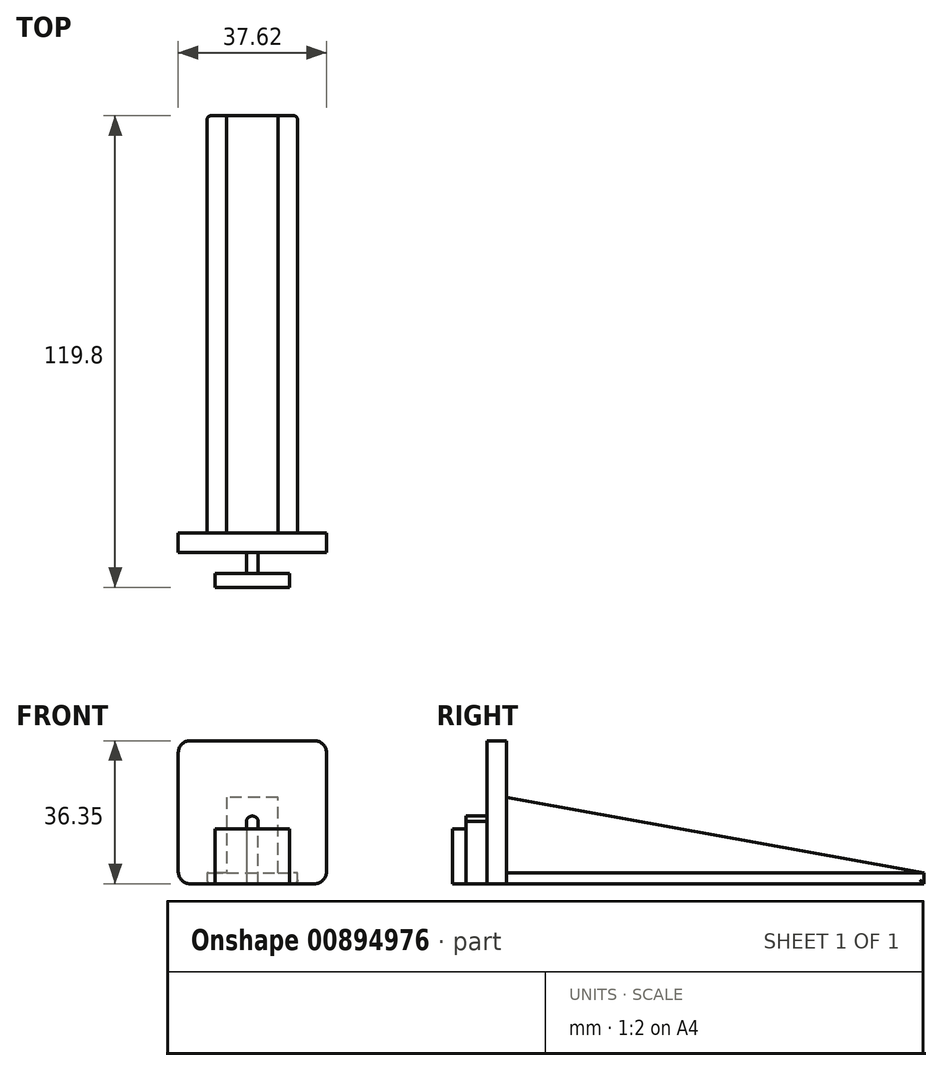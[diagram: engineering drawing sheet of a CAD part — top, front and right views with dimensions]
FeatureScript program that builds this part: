
annotation { "Feature Type Name" : "Feature", "Feature Type Description" : "" }
export const myFeature = defineFeature(function(context is Context, id is Id, definition is map)
    precondition{}
    {
        {
            var Q0;
            Q0=qCreatedBy(makeId("Front.planeOp"),FACE);
            var sketch = newSketch(context, id + "F0", { "sketchPlane" : qUnion([Q0])});
            skLineSegment(sketch, "E0", {"start": v(0, 0) * mm, "end": v(0, 36.35) * mm});
            skLineSegment(sketch, "E1", {"start": v(0, 36.35) * mm, "end": v(37.62, 36.35) * mm});
            skLineSegment(sketch, "E2", {"start": v(37.62, 36.35) * mm, "end": v(37.62, 0) * mm});
            skLineSegment(sketch, "E3", {"start": v(37.62, 0) * mm, "end": v(0, 0) * mm});
            skSolve(sketch);
        }
        {
            var Q0;
            Q0 = qSketchRegion(id + "F0", true);
            extrude(context, id + "F1", {"entities" : qUnion([Q0]), "depth" : 5 * mm, "offsetDistance" : 25 * mm});
        }
        {
            var Q0;
            Q0=makeQuery(id+"F1.opExtrude","CAP_FACE",FACE,{"disambiguationData":[OSD([sQuery(id+"F0.wireOp",EDGE,"E0"),sQuery(id+"F0.wireOp",EDGE,"E1"),sQuery(id+"F0.wireOp",EDGE,"E2"),sQuery(id+"F0.wireOp",EDGE,"E3")])],"isStart":false});
            var sketch = newSketch(context, id + "F2", { "sketchPlane" : qUnion([Q0])});
            skLineSegment(sketch, "E4", {"start": v(17.3, 0) * mm, "end": v(20.31, 0) * mm});
            skLineSegment(sketch, "E5", {"start": v(20.3, 0) * mm, "end": v(20.3, 17.2) * mm});
            skLineSegment(sketch, "E6", {"start": v(20.3, 17.2) * mm, "end": v(17.31, 17.2) * mm});
            skLineSegment(sketch, "E7", {"start": v(17.3, 17.2) * mm, "end": v(17.3, 0) * mm});
            skPoint(sketch, "E8", {"position": v(18.8, 0) * mm});
            skSolve(sketch);
        }
        {
            var Q0;
            Q0=makeQuery(id+"F2.imprint","IMPRINT",FACE,{"disambiguationData":[TD([[makeQuery(id+"F2.imprint","IMPRINT",EDGE,{"derivedFrom":sQuery(id+"F2.wireOp",EDGE,"E4")}),-1.0]])]});
            extrude(context, id + "F3", {"entities" : qUnion([Q0]), "operationType" : NewBodyOperationType.ADD, "depth" : 5.3 * mm, "offsetDistance" : 25 * mm});
        }
        {
            var Q0;
            Q0=makeQuery(id+"F3.opExtrude","CAP_FACE",FACE,{"disambiguationData":[OSD([sQuery(id+"F2.wireOp",EDGE,"E4"),sQuery(id+"F2.wireOp",EDGE,"E5"),sQuery(id+"F2.wireOp",EDGE,"E6"),sQuery(id+"F2.wireOp",EDGE,"E7")])],"isStart":false});
            var sketch = newSketch(context, id + "F4", { "sketchPlane" : qUnion([Q0])});
            skLineSegment(sketch, "E9", {"start": v(9.3, 0) * mm, "end": v(28.31, 0) * mm});
            skPoint(sketch, "E10", {"position": v(18.8, 0) * mm});
            skLineSegment(sketch, "E11", {"start": v(9.3, 0) * mm, "end": v(9.3, 14) * mm});
            skLineSegment(sketch, "E12", {"start": v(9.3, 14) * mm, "end": v(28.3, 14) * mm});
            skLineSegment(sketch, "E13", {"start": v(28.3, 14) * mm, "end": v(28.3, 0) * mm});
            skSolve(sketch);
        }
        {
            var Q0;
            Q0 = qSketchRegion(id + "F4", true);
            extrude(context, id + "F5", {"entities" : qUnion([Q0]), "operationType" : NewBodyOperationType.ADD, "depth" : 3.5 * mm, "offsetDistance" : 25 * mm});
        }
        {
            var Q0;
            Q0=makeQuery(id+"F1.opExtrude","CAP_FACE",FACE,{"disambiguationData":[OSD([sQuery(id+"F0.wireOp",EDGE,"E0"),sQuery(id+"F0.wireOp",EDGE,"E1"),sQuery(id+"F0.wireOp",EDGE,"E2"),sQuery(id+"F0.wireOp",EDGE,"E3")])],"isStart":true});
            var sketch = newSketch(context, id + "F6", { "sketchPlane" : qUnion([Q0])});
            skPoint(sketch, "E14", {"position": v(-18.8, 0) * mm});
            skLineSegment(sketch, "E15", {"start": v(-30.3, 0) * mm, "end": v(-7.31, 0) * mm});
            skLineSegment(sketch, "E16", {"start": v(-30.3, 0) * mm, "end": v(-30.3, 22) * mm});
            skLineSegment(sketch, "E17", {"start": v(-30.3, 22) * mm, "end": v(-7.3, 22) * mm});
            skLineSegment(sketch, "E18", {"start": v(-7.3, 22) * mm, "end": v(-7.3, 0) * mm});
            skSolve(sketch);
        }
        {
            var Q0;
            Q0=makeQuery(id+"F6.imprint","IMPRINT",FACE,{"disambiguationData":[TD([[makeQuery(id+"F6.imprint","IMPRINT",EDGE,{"derivedFrom":sQuery(id+"F6.wireOp",EDGE,"E15")}),1.0]])]});
            extrude(context, id + "F7", {"entities" : qUnion([Q0]), "operationType" : NewBodyOperationType.ADD, "depth" : 106 * mm, "offsetDistance" : 25 * mm});
        }
        {
            var Q0;
            Q0=makeQuery(id+"F7.opExtrude","SWEPT_FACE",FACE,{"disambiguationData":[OSD([sQuery(id+"F6.wireOp",EDGE,"E16")])]});
            var sketch = newSketch(context, id + "F8", { "sketchPlane" : qUnion([Q0])});
            skLineSegment(sketch, "E19", {"start": v(0, 22) * mm, "end": v(106, 2.8) * mm});
            skSolve(sketch);
        }
        {
            var Q0;
            {var subQ0=sQuery(id+"F8.wireOp",EDGE,"E19");Q0=makeQuery(id+"F8.imprint","IMPRINT",FACE,{"disambiguationData":[TD([[makeQuery(id+"F8.imprint","IMPRINT",EDGE,{"derivedFrom":subQ0}),1.0]])]});}
            extrude(context, id + "F9", {"entities" : qUnion([Q0]), "operationType" : NewBodyOperationType.REMOVE, "oppositeDirection" : true, "depth" : 25 * mm, "offsetDistance" : 25 * mm});
        }
        {
            var Q0;
            Q0=makeQuery(id+"F7.opExtrude","SWEPT_FACE",FACE,{"disambiguationData":[OSD([sQuery(id+"F6.wireOp",EDGE,"E16")])]});
            var sketch = newSketch(context, id + "F10", { "sketchPlane" : qUnion([Q0])});
            skLineSegment(sketch, "E20", {"start": v(106, 2.8) * mm, "end": v(0, 2.8) * mm});
            skSolve(sketch);
        }
        {
            var Q0;
            {var subQ0=sQuery(id+"F10.wireOp",EDGE,"E20");Q0=makeQuery(id+"F10.imprint","IMPRINT",FACE,{"disambiguationData":[TD([[makeQuery(id+"F10.imprint","IMPRINT",EDGE,{"derivedFrom":subQ0}),-1.0]])]});}
            extrude(context, id + "F11", {"entities" : qUnion([Q0]), "operationType" : NewBodyOperationType.REMOVE, "oppositeDirection" : true, "depth" : 5 * mm, "offsetDistance" : 25 * mm});
        }
        {
            var Q0;
            Q0=makeQuery(id+"F7.opExtrude","SWEPT_FACE",FACE,{"disambiguationData":[OSD([sQuery(id+"F6.wireOp",EDGE,"E18")])]});
            var sketch = newSketch(context, id + "F12", { "sketchPlane" : qUnion([Q0])});
            skLineSegment(sketch, "E21", {"start": v(-106, 2.8) * mm, "end": v(0, 2.8) * mm});
            skSolve(sketch);
        }
        {
            var Q0;
            {var subQ0=sQuery(id+"F12.wireOp",EDGE,"E21");Q0=makeQuery(id+"F12.imprint","IMPRINT",FACE,{"disambiguationData":[TD([[makeQuery(id+"F12.imprint","IMPRINT",EDGE,{"derivedFrom":subQ0}),1.0]])]});}
            extrude(context, id + "F13", {"entities" : qUnion([Q0]), "operationType" : NewBodyOperationType.REMOVE, "oppositeDirection" : true, "depth" : 5 * mm, "offsetDistance" : 25 * mm});
        }
        {
            var Q0;
            Q0=makeQuery(id+"F1.opExtrude","SWEPT_EDGE",EDGE,{"disambiguationData":[OSD([sQuery(id+"F0.wireOp",EDGE,"E2"),sQuery(id+"F0.wireOp",EDGE,"E3")])]});
            var Q1;
            Q1=makeQuery(id+"F1.opExtrude","SWEPT_EDGE",EDGE,{"disambiguationData":[OSD([sQuery(id+"F0.wireOp",EDGE,"E1"),sQuery(id+"F0.wireOp",EDGE,"E2")])]});
            var Q2;
            Q2=makeQuery(id+"F1.opExtrude","SWEPT_EDGE",EDGE,{"disambiguationData":[OSD([sQuery(id+"F0.wireOp",EDGE,"E0"),sQuery(id+"F0.wireOp",EDGE,"E1")])]});
            var Q3;
            Q3=makeQuery(id+"F1.opExtrude","SWEPT_EDGE",EDGE,{"disambiguationData":[OSD([sQuery(id+"F0.wireOp",EDGE,"E0"),sQuery(id+"F0.wireOp",EDGE,"E3")])]});
            fillet(context, id + "F14", {"entities" : qUnion([Q0, Q1, Q2, Q3]), "radius" : 3 * mm, "tangentPropagation" : true, "allowEdgeOverflow" : false});
        }
        {
            var Q0;
            Q0=makeQuery(id+"F3.opExtrude","CAP_FACE",FACE,{"disambiguationData":[OSD([sQuery(id+"F2.wireOp",EDGE,"E4"),sQuery(id+"F2.wireOp",EDGE,"E5"),sQuery(id+"F2.wireOp",EDGE,"E6"),sQuery(id+"F2.wireOp",EDGE,"E7")])],"isStart":false});
            var sketch = newSketch(context, id + "F15", { "sketchPlane" : qUnion([Q0])});
            skPoint(sketch, "E22.third.point", {"position": v(18.8, 17.2) * mm});
            skCircle(sketch, "E23", {"center": v(18.8, 15.7) * mm, "radius": 1.5 * mm});
            skPoint(sketch, "E23.first.point", {"position": v(17.3, 15.6) * mm});
            skPoint(sketch, "E23.second.point", {"position": v(20.3, 15.6) * mm});
            skSolve(sketch);
        }
        {
            var Q0;
            {var subQ0=sQuery(id+"F15.wireOp",EDGE,"E23");var subQ1=sQuery(id+"F2.wireOp",EDGE,"E6");var subQ2=makeQuery(id+"F3.opExtrude","CAP_EDGE",EDGE,{"disambiguationData":[OSD([subQ1])],"isStart":false});var subQ3=makeQuery(id+"F15.imprint","INTERSECT",VERTEX,{"derivedFrom":[subQ2,subQ0]});Q0=makeQuery(id+"F15.imprint","IMPRINT",FACE,{"disambiguationData":[TD([[makeQuery(id+"F15.imprint","IMPRINT",EDGE,{"disambiguationData":[TD([[subQ3,-1.0]])],"derivedFrom":subQ0}),-1.0]])]});}
            var Q1;
            {var subQ0=sQuery(id+"F15.wireOp",EDGE,"E23");var subQ1=sQuery(id+"F2.wireOp",EDGE,"E6");var subQ2=makeQuery(id+"F3.opExtrude","CAP_EDGE",EDGE,{"disambiguationData":[OSD([subQ1])],"isStart":false});var subQ3=makeQuery(id+"F15.imprint","INTERSECT",VERTEX,{"derivedFrom":[subQ2,subQ0]});Q1=makeQuery(id+"F15.imprint","IMPRINT",FACE,{"disambiguationData":[TD([[makeQuery(id+"F15.imprint","IMPRINT",EDGE,{"disambiguationData":[TD([[subQ3,1.0]])],"derivedFrom":subQ0}),-1.0]])]});}
            var Q2;
            Q2=makeQuery(id+"F1.opExtrude","CAP_FACE",FACE,{"disambiguationData":[OSD([sQuery(id+"F0.wireOp",EDGE,"E0"),sQuery(id+"F0.wireOp",EDGE,"E1"),sQuery(id+"F0.wireOp",EDGE,"E2"),sQuery(id+"F0.wireOp",EDGE,"E3")])],"isStart":false});
            extrude(context, id + "F16", {"entities" : qUnion([Q0, Q1]), "operationType" : NewBodyOperationType.REMOVE, "endBound" : BoundingType.UP_TO_SURFACE, "oppositeDirection" : true, "depth" : 25 * mm, "endBoundEntityFace" : qUnion([Q2]), "offsetDistance" : 25 * mm});
        }
        {
            var Q0;
            Q0=makeQuery(id+"F7.opExtrude","CAP_EDGE",EDGE,{"disambiguationData":[OSD([sQuery(id+"F6.wireOp",EDGE,"E16")])],"isStart":false});
            var Q1;
            Q1=makeQuery(id+"F7.opExtrude","CAP_EDGE",EDGE,{"disambiguationData":[OSD([sQuery(id+"F6.wireOp",EDGE,"E18")])],"isStart":false});
            var Q2;
            Q2=makeQuery(id+"F13.boolean.opBoolean","COPY",EDGE,{"derivedFrom":makeQuery(id+"F13.opExtrude","CAP_EDGE",EDGE,{"disambiguationData":[OSD([sQuery(id+"F12.wireOp",EDGE,"E21")])],"isStart":true})});
            var Q3;
            Q3=makeQuery(id+"F7.opExtrude","SWEPT_EDGE",EDGE,{"disambiguationData":[OSD([sQuery(id+"F0.wireOp",EDGE,"E3"),sQuery(id+"F6.wireOp",EDGE,"E15"),sQuery(id+"F6.wireOp",EDGE,"E18")])]});
            var Q4;
            Q4=makeQuery(id+"F13.boolean.opBoolean","COPY",EDGE,{"derivedFrom":makeQuery(id+"F13.opExtrude","CAP_EDGE",EDGE,{"disambiguationData":[OSD([sQuery(id+"F6.wireOp",EDGE,"E18"),sQuery(id+"F8.wireOp",EDGE,"E19")])],"isStart":false})});
            var Q5;
            Q5=makeQuery(id+"F11.boolean.opBoolean","COPY",EDGE,{"derivedFrom":makeQuery(id+"F11.opExtrude","CAP_EDGE",EDGE,{"disambiguationData":[OSD([sQuery(id+"F8.wireOp",EDGE,"E19")])],"isStart":false})});
            var Q6;
            Q6=makeQuery(id+"F11.boolean.opBoolean","COPY",EDGE,{"derivedFrom":makeQuery(id+"F11.opExtrude","CAP_EDGE",EDGE,{"disambiguationData":[OSD([sQuery(id+"F10.wireOp",EDGE,"E20")])],"isStart":true})});
            var Q7;
            Q7=makeQuery(id+"F7.opExtrude","SWEPT_EDGE",EDGE,{"disambiguationData":[OSD([sQuery(id+"F0.wireOp",EDGE,"E3"),sQuery(id+"F6.wireOp",EDGE,"E15"),sQuery(id+"F6.wireOp",EDGE,"E16")])]});
            fillet(context, id + "F17", {"entities" : qUnion([Q0, Q1, Q2, Q3, Q4, Q5, Q6, Q7]), "radius" : 1 * mm, "tangentPropagation" : true, "allowEdgeOverflow" : false});
        }
    });
